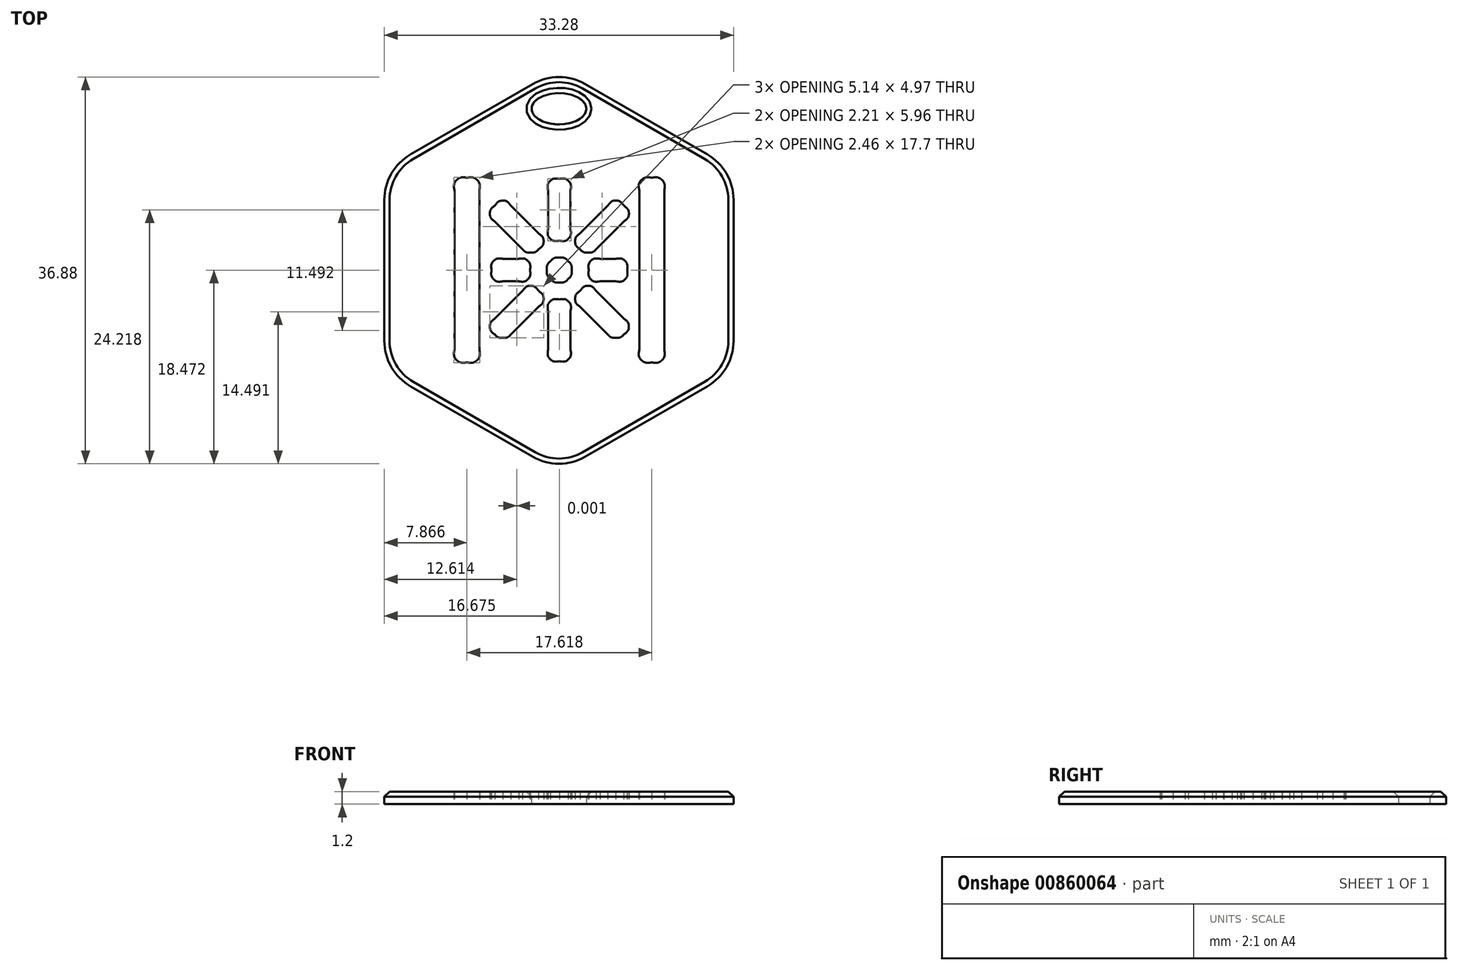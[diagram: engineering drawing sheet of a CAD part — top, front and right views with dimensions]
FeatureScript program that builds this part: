
annotation { "Feature Type Name" : "Feature", "Feature Type Description" : "" }
export const myFeature = defineFeature(function(context is Context, id is Id, definition is map)
    precondition{}
    {
        {
            var Q0;
            Q0=qCreatedBy(makeId("Top.planeOp"),FACE);
            var sketch = newSketch(context, id + "F0", { "sketchPlane" : qUnion([Q0])});
            skCircle(sketch, "E0.cCircle", {"center": v(0, 0) * mm, "radius": 16.64 * mm, "construction": true});
            skLineSegment(sketch, "E0.0", {"start": v(16.64, 6.72) * mm, "end": v(16.64, -6.72) * mm});
            skLineSegment(sketch, "E0.1", {"start": v(14.14, -11.05) * mm, "end": v(2.5, -17.77) * mm});
            skLineSegment(sketch, "E0.2", {"start": v(-2.5, -17.77) * mm, "end": v(-14.14, -11.05) * mm});
            skLineSegment(sketch, "E0.3", {"start": v(-16.64, -6.72) * mm, "end": v(-16.64, 6.72) * mm});
            skLineSegment(sketch, "E0.4", {"start": v(-14.14, 11.05) * mm, "end": v(-2.5, 17.77) * mm});
            skLineSegment(sketch, "E0.5", {"start": v(2.5, 17.77) * mm, "end": v(14.14, 11.05) * mm});
            skPoint(sketch, "E0.0.midPoint", {"position": v(16.64, 0) * mm});
            skPoint(sketch, "E1.visualSharp", {"position": v(-16.64, 9.6) * mm});
            skArc(sketch, "E1.filletArc", {"start": v(-14.14, 11.05) * mm, "mid": v(-15.97, 9.22) * mm, "end": v(-16.64, 6.72) * mm});
            skPoint(sketch, "E2.visualSharp", {"position": v(0, 19.22) * mm});
            skArc(sketch, "E2.filletArc", {"start": v(2.5, 17.77) * mm, "mid": v(0, 18.44) * mm, "end": v(-2.5, 17.77) * mm});
            skPoint(sketch, "E3.visualSharp", {"position": v(16.64, 9.6) * mm});
            skArc(sketch, "E3.filletArc", {"start": v(16.64, 6.72) * mm, "mid": v(15.97, 9.22) * mm, "end": v(14.14, 11.05) * mm});
            skPoint(sketch, "E4.visualSharp", {"position": v(16.64, -9.6) * mm});
            skArc(sketch, "E4.filletArc", {"start": v(14.14, -11.05) * mm, "mid": v(15.97, -9.22) * mm, "end": v(16.64, -6.72) * mm});
            skPoint(sketch, "E5.visualSharp", {"position": v(0, -19.22) * mm});
            skArc(sketch, "E5.filletArc", {"start": v(-2.5, -17.77) * mm, "mid": v(0, -18.44) * mm, "end": v(2.5, -17.77) * mm});
            skPoint(sketch, "E6.visualSharp", {"position": v(-16.64, -9.6) * mm});
            skArc(sketch, "E6.filletArc", {"start": v(-16.64, -6.72) * mm, "mid": v(-15.97, -9.22) * mm, "end": v(-14.14, -11.05) * mm});
            skPoint(sketch, "E7.visualSharp", {"position": v(-14.64, 8.45) * mm});
            skPoint(sketch, "E8.visualSharp", {"position": v(0, 16.9) * mm});
            skPoint(sketch, "E9.visualSharp", {"position": v(14.64, 8.45) * mm});
            skPoint(sketch, "E10.visualSharp", {"position": v(14.64, -8.45) * mm});
            skPoint(sketch, "E11.visualSharp", {"position": v(0, -16.9) * mm});
            skPoint(sketch, "E12.visualSharp", {"position": v(-14.64, -8.45) * mm});
            skFitSpline(sketch, "E13", {"points": [v(-5.35, -6.43) * mm, v(-5.63, -6.43) * mm, v(-5.9, -6.32) * mm, v(-6.1, -6.11) * mm]});
            skFitSpline(sketch, "E14", {"points": [v(-6.1, -6.11) * mm, v(-6.53, -5.7) * mm, v(-6.53, -5.02) * mm, v(-6.1, -4.6) * mm]});
            skFitSpline(sketch, "E15", {"points": [v(-3.47, -1.95) * mm, v(-3.05, -1.53) * mm, v(-2.37, -1.53) * mm, v(-1.94, -1.95) * mm]});
            skFitSpline(sketch, "E16", {"points": [v(-1.94, -1.95) * mm, v(-1.53, -2.37) * mm, v(-1.53, -3.05) * mm, v(-1.94, -3.47) * mm]});
            skLineSegment(sketch, "E17", {"start": v(-6.1, -4.6) * mm, "end": v(-3.47, -1.95) * mm});
            skFitSpline(sketch, "E18", {"points": [v(-4.6, -6.11) * mm, v(-4.8, -6.32) * mm, v(-5.07, -6.43) * mm, v(-5.35, -6.43) * mm]});
            skLineSegment(sketch, "E19", {"start": v(-1.94, -3.47) * mm, "end": v(-4.6, -6.11) * mm});
            skFitSpline(sketch, "E20", {"points": [v(3.91, -1.04) * mm, v(3.32, -1.04) * mm, v(2.84, -0.56) * mm, v(2.84, 0.03) * mm]});
            skFitSpline(sketch, "E21", {"points": [v(2.84, 0.03) * mm, v(2.84, 0.63) * mm, v(3.32, 1.1) * mm, v(3.91, 1.1) * mm]});
            skLineSegment(sketch, "E22", {"start": v(5.42, -1.04) * mm, "end": v(3.91, -1.04) * mm});
            skFitSpline(sketch, "E23", {"points": [v(5.42, 1.1) * mm, v(6.01, 1.1) * mm, v(6.5, 0.63) * mm, v(6.5, 0.03) * mm]});
            skFitSpline(sketch, "E24", {"points": [v(6.5, 0.03) * mm, v(6.5, -0.56) * mm, v(6.01, -1.04) * mm, v(5.42, -1.04) * mm]});
            skLineSegment(sketch, "E25", {"start": v(3.91, 1.1) * mm, "end": v(5.42, 1.1) * mm});
            skFitSpline(sketch, "E26", {"points": [v(-5.34, -1.04) * mm, v(-5.94, -1.04) * mm, v(-6.42, -0.56) * mm, v(-6.42, 0.03) * mm]});
            skFitSpline(sketch, "E27", {"points": [v(-6.42, 0.03) * mm, v(-6.42, 0.63) * mm, v(-5.94, 1.1) * mm, v(-5.34, 1.1) * mm]});
            skLineSegment(sketch, "E28", {"start": v(-3.84, -1.04) * mm, "end": v(-5.34, -1.04) * mm});
            skFitSpline(sketch, "E29", {"points": [v(-3.84, 1.1) * mm, v(-3.25, 1.1) * mm, v(-2.77, 0.63) * mm, v(-2.77, 0.03) * mm]});
            skFitSpline(sketch, "E30", {"points": [v(-2.77, 0.03) * mm, v(-2.77, -0.56) * mm, v(-3.25, -1.04) * mm, v(-3.84, -1.04) * mm]});
            skFitSpline(sketch, "E31", {"points": [v(5.42, -6.43) * mm, v(5.14, -6.43) * mm, v(4.87, -6.32) * mm, v(4.66, -6.11) * mm]});
            skLineSegment(sketch, "E32", {"start": v(-5.34, 1.1) * mm, "end": v(-3.84, 1.1) * mm});
            skFitSpline(sketch, "E33", {"points": [v(2.02, -3.47) * mm, v(1.6, -3.05) * mm, v(1.6, -2.37) * mm, v(2.02, -1.95) * mm]});
            skFitSpline(sketch, "E34", {"points": [v(2.02, -1.95) * mm, v(2.44, -1.53) * mm, v(3.12, -1.53) * mm, v(3.54, -1.95) * mm]});
            skLineSegment(sketch, "E35", {"start": v(4.66, -6.11) * mm, "end": v(2.02, -3.47) * mm});
            skFitSpline(sketch, "E36", {"points": [v(6.18, -4.6) * mm, v(6.6, -5.01) * mm, v(6.6, -5.7) * mm, v(6.18, -6.11) * mm]});
            skFitSpline(sketch, "E37", {"points": [v(6.18, -6.11) * mm, v(5.97, -6.32) * mm, v(5.7, -6.43) * mm, v(5.42, -6.43) * mm]});
            skFitSpline(sketch, "E38", {"points": [v(0.04, -8.66) * mm, v(-0.56, -8.66) * mm, v(-1.04, -8.18) * mm, v(-1.04, -7.59) * mm]});
            skLineSegment(sketch, "E39", {"start": v(3.54, -1.95) * mm, "end": v(6.18, -4.6) * mm});
            skFitSpline(sketch, "E40", {"points": [v(-1.04, -3.85) * mm, v(-1.04, -3.25) * mm, v(-0.56, -2.77) * mm, v(0.04, -2.77) * mm]});
            skFitSpline(sketch, "E41", {"points": [v(0.04, -2.77) * mm, v(0.63, -2.77) * mm, v(1.1, -3.25) * mm, v(1.1, -3.85) * mm]});
            skLineSegment(sketch, "E42", {"start": v(-1.04, -7.59) * mm, "end": v(-1.04, -3.85) * mm});
            skFitSpline(sketch, "E43", {"points": [v(1.1, -7.59) * mm, v(1.1, -8.18) * mm, v(0.63, -8.66) * mm, v(0.04, -8.66) * mm]});
            skFitSpline(sketch, "E44", {"points": [v(0.04, 2.83) * mm, v(-0.56, 2.83) * mm, v(-1.04, 3.32) * mm, v(-1.04, 3.9) * mm]});
            skLineSegment(sketch, "E45", {"start": v(1.1, -3.85) * mm, "end": v(1.1, -7.59) * mm});
            skFitSpline(sketch, "E46", {"points": [v(-1.04, 7.65) * mm, v(-1.04, 8.24) * mm, v(-0.56, 8.72) * mm, v(0.04, 8.72) * mm]});
            skFitSpline(sketch, "E47", {"points": [v(0.04, 8.72) * mm, v(0.63, 8.72) * mm, v(1.1, 8.24) * mm, v(1.1, 7.65) * mm]});
            skLineSegment(sketch, "E48", {"start": v(-1.04, 3.9) * mm, "end": v(-1.04, 7.65) * mm});
            skFitSpline(sketch, "E49", {"points": [v(1.1, 3.9) * mm, v(1.1, 3.32) * mm, v(0.63, 2.83) * mm, v(0.04, 2.83) * mm]});
            skFitSpline(sketch, "E50", {"points": [v(8.84, -8.78) * mm, v(8.18, -8.78) * mm, v(7.65, -8.24) * mm, v(7.65, -7.59) * mm]});
            skLineSegment(sketch, "E51", {"start": v(1.1, 7.65) * mm, "end": v(1.1, 3.9) * mm});
            skFitSpline(sketch, "E52", {"points": [v(7.65, 7.65) * mm, v(7.65, 8.3) * mm, v(8.18, 8.84) * mm, v(8.84, 8.84) * mm]});
            skFitSpline(sketch, "E53", {"points": [v(8.84, 8.84) * mm, v(9.5, 8.84) * mm, v(10.04, 8.3) * mm, v(10.04, 7.65) * mm]});
            skLineSegment(sketch, "E54", {"start": v(7.65, -7.59) * mm, "end": v(7.65, 7.65) * mm});
            skFitSpline(sketch, "E55", {"points": [v(10.04, -7.59) * mm, v(10.04, -8.24) * mm, v(9.5, -8.78) * mm, v(8.84, -8.78) * mm]});
            skFitSpline(sketch, "E56", {"points": [v(2.78, 1.7) * mm, v(2.5, 1.7) * mm, v(2.23, 1.8) * mm, v(2.02, 2.01) * mm]});
            skFitSpline(sketch, "E57", {"points": [v(2.02, 2.01) * mm, v(1.6, 2.43) * mm, v(1.6, 3.11) * mm, v(2.02, 3.53) * mm]});
            skLineSegment(sketch, "E58", {"start": v(10.04, 7.65) * mm, "end": v(10.04, -7.59) * mm});
            skFitSpline(sketch, "E59", {"points": [v(4.66, 6.18) * mm, v(5.08, 6.6) * mm, v(5.76, 6.6) * mm, v(6.18, 6.18) * mm]});
            skFitSpline(sketch, "E60", {"points": [v(6.18, 6.18) * mm, v(6.6, 5.76) * mm, v(6.6, 5.08) * mm, v(6.18, 4.66) * mm]});
            skLineSegment(sketch, "E61", {"start": v(2.02, 3.53) * mm, "end": v(4.66, 6.18) * mm});
            skFitSpline(sketch, "E62", {"points": [v(3.54, 2.02) * mm, v(3.33, 1.8) * mm, v(3.05, 1.7) * mm, v(2.78, 1.7) * mm]});
            skFitSpline(sketch, "E63", {"points": [v(-2.7, 1.7) * mm, v(-2.98, 1.7) * mm, v(-3.25, 1.8) * mm, v(-3.47, 2.01) * mm]});
            skLineSegment(sketch, "E64", {"start": v(6.18, 4.66) * mm, "end": v(3.54, 2.02) * mm});
            skFitSpline(sketch, "E65", {"points": [v(-6.1, 4.66) * mm, v(-6.53, 5.08) * mm, v(-6.53, 5.76) * mm, v(-6.1, 6.18) * mm]});
            skFitSpline(sketch, "E66", {"points": [v(-6.1, 6.18) * mm, v(-5.69, 6.6) * mm, v(-5, 6.6) * mm, v(-4.6, 6.18) * mm]});
            skLineSegment(sketch, "E67", {"start": v(-3.47, 2.01) * mm, "end": v(-6.1, 4.66) * mm});
            skFitSpline(sketch, "E68", {"points": [v(-1.95, 3.53) * mm, v(-1.53, 3.11) * mm, v(-1.53, 2.43) * mm, v(-1.95, 2.01) * mm]});
            skFitSpline(sketch, "E69", {"points": [v(-1.95, 2.01) * mm, v(-2.15, 1.8) * mm, v(-2.43, 1.7) * mm, v(-2.7, 1.7) * mm]});
            skFitSpline(sketch, "E70", {"points": [v(0.04, -1.16) * mm, v(-0.28, -1.16) * mm, v(-0.59, -1.03) * mm, v(-0.8, -0.81) * mm]});
            skFitSpline(sketch, "E71", {"points": [v(-0.8, -0.81) * mm, v(-1.03, -0.59) * mm, v(-1.16, -0.28) * mm, v(-1.16, 0.03) * mm]});
            skFitSpline(sketch, "E72", {"points": [v(-1.16, 0.03) * mm, v(-1.16, 0.35) * mm, v(-1.03, 0.65) * mm, v(-0.8, 0.87) * mm]});
            skFitSpline(sketch, "E73", {"points": [v(-0.8, 0.87) * mm, v(-0.59, 1.1) * mm, v(-0.28, 1.22) * mm, v(0.04, 1.22) * mm]});
            skFitSpline(sketch, "E74", {"points": [v(0.04, 1.22) * mm, v(0.35, 1.22) * mm, v(0.66, 1.1) * mm, v(0.88, 0.87) * mm]});
            skFitSpline(sketch, "E75", {"points": [v(0.88, 0.87) * mm, v(1.1, 0.65) * mm, v(1.23, 0.35) * mm, v(1.23, 0.03) * mm]});
            skFitSpline(sketch, "E76", {"points": [v(1.23, 0.03) * mm, v(1.23, -0.28) * mm, v(1.1, -0.59) * mm, v(0.88, -0.81) * mm]});
            skFitSpline(sketch, "E77", {"points": [v(0.88, -0.81) * mm, v(0.66, -1.03) * mm, v(0.35, -1.16) * mm, v(0.04, -1.16) * mm]});
            skFitSpline(sketch, "E78", {"points": [v(-8.77, -8.78) * mm, v(-9.43, -8.78) * mm, v(-9.96, -8.24) * mm, v(-9.96, -7.59) * mm]});
            skLineSegment(sketch, "E79", {"start": v(-4.6, 6.18) * mm, "end": v(-1.95, 3.53) * mm});
            skFitSpline(sketch, "E80", {"points": [v(-9.96, 7.65) * mm, v(-9.96, 8.3) * mm, v(-9.43, 8.84) * mm, v(-8.77, 8.84) * mm]});
            skFitSpline(sketch, "E81", {"points": [v(-8.77, 8.84) * mm, v(-8.11, 8.84) * mm, v(-7.58, 8.3) * mm, v(-7.58, 7.65) * mm]});
            skLineSegment(sketch, "E82", {"start": v(-9.96, -7.59) * mm, "end": v(-9.96, 7.65) * mm});
            skFitSpline(sketch, "E83", {"points": [v(-7.58, -7.59) * mm, v(-7.58, -8.24) * mm, v(-8.11, -8.78) * mm, v(-8.77, -8.78) * mm]});
            skLineSegment(sketch, "E84", {"start": v(-7.58, 7.65) * mm, "end": v(-7.58, -7.59) * mm});
            skEllipse(sketch, "E85", {"center": v(0, 15.41) * mm, "majorRadius": 2.6 * mm, "minorRadius": 1.5 * mm, "majorAxis": v(1, 0)});
            skSolve(sketch);
        }
        {
            var Q0;
            Q0=qSketchRegion(id+"F0",true);
            extrude(context, id + "F1", {"entities" : qUnion([Q0]), "depth" : 1.2 * mm});
        }
        {
            var Q0;
            Q0=makeQuery(id+"F1.opExtrude","CAP_EDGE",EDGE,{"disambiguationData":[OSD([sQuery(id+"F0.wireOp",EDGE,"E0.2")])],"isStart":false});
            chamfer(context, id + "F2", {"entities" : qUnion([Q0]), "width" : 0.5 * mm, "tangentPropagation" : true});
        }
        {
            var Q0;
            Q0=makeQuery(id+"F1.opExtrude","CAP_EDGE",EDGE,{"disambiguationData":[OSD([sQuery(id+"F0.wireOp",EDGE,"E85")])],"isStart":false});
            chamfer(context, id + "F3", {"entities" : qUnion([Q0]), "width" : 0.5 * mm, "tangentPropagation" : true});
        }
    });
